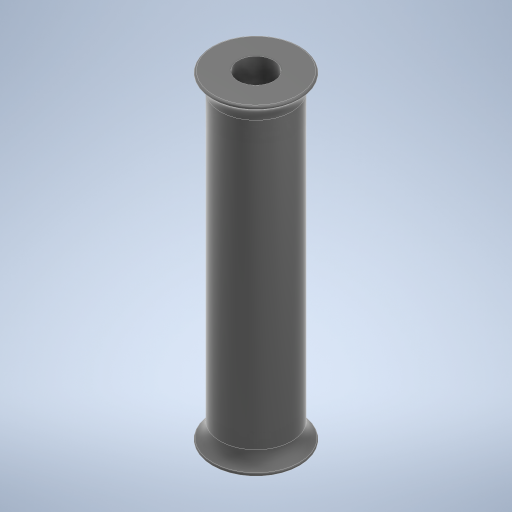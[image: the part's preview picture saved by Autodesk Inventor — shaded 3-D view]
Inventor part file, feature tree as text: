
AUTODESK INVENTOR PART (.ipt)
format: ipt  version: 2024 (Build 280153000, 153)  size: 279,552 bytes
history: native  units: in
note: dims shown in document units (in); Inventor stores cm internally (conversion verified against a paired STEP export)
features: sketch x2, other x1, revolve x1, hole x1
ambient origin geometry x8: Origin, YZ Plane, XZ Plane, XY Plane, X Axis, Y Axis, Z Axis, Center Point
bodies: Body1 (feature_tree)
feature tree (5):
  other  "Main Body"
  revolve  "Revolution1"  [1 undecoded]
  hole  "Hole1"  [1 undecoded]
  sketch  "Sketch1"  dims[d0=0.1969in d1=1.5748in]
  sketch  "Sketch2"  dims[d2=0.1969in d3=0.2953in d4=0.0098in d5=0.0984in d6=0.1969in d7=0.2953in d8=0.0098in d9=90.0deg d10=0.1969in d11=0.2953in d12=0.1476in d13=0.0984in d14=90.0deg d15=0.3937in d16=0.8108in]
note: 2 required parameter values undecoded (feature->parameter linkage not recoverable at this tier; creation-order binding heuristic only, values carry confidence <= 0.55)